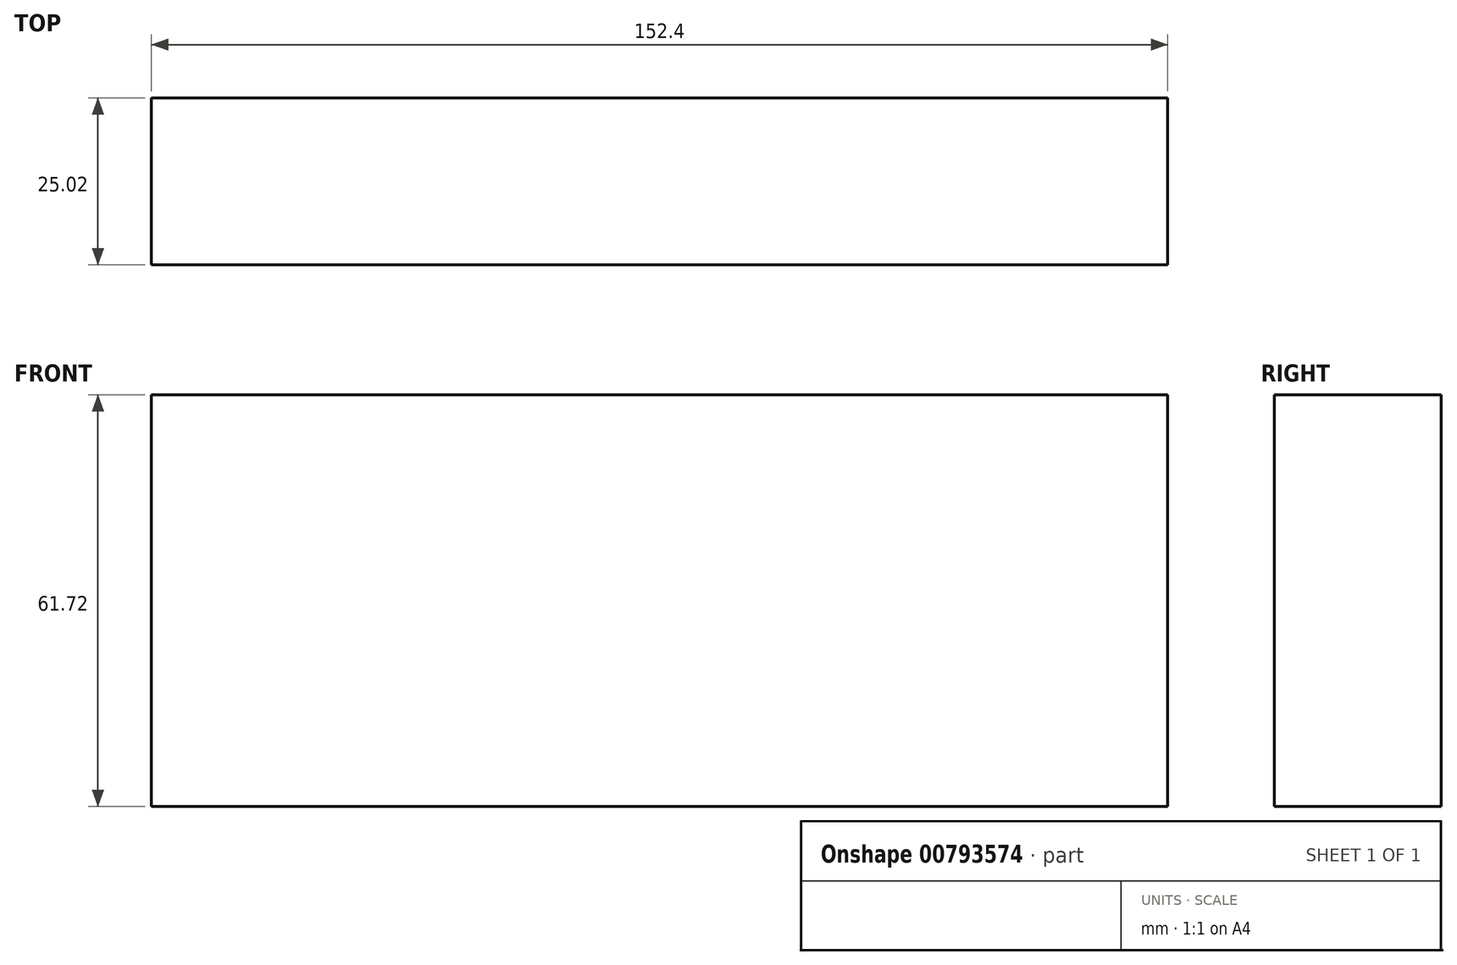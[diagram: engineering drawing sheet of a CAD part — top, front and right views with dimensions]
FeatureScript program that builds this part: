
annotation { "Feature Type Name" : "Feature", "Feature Type Description" : "" }
export const myFeature = defineFeature(function(context is Context, id is Id, definition is map)
    precondition{}
    {
        {
            var Q0;
            Q0=qCreatedBy(makeId("Front.planeOp"),FACE);
            var sketch = newSketch(context, id + "F0", { "sketchPlane" : qUnion([Q0])});
            skLineSegment(sketch, "E0.bottom", {"start": v(0, 0) * mm, "end": v(152.4, 0) * mm});
            skLineSegment(sketch, "E0.top", {"start": v(0, 61.72) * mm, "end": v(152.4, 61.72) * mm});
            skLineSegment(sketch, "E0.left", {"start": v(0, 0) * mm, "end": v(0, 61.72) * mm});
            skLineSegment(sketch, "E0.right", {"start": v(152.4, 0) * mm, "end": v(152.4, 61.72) * mm});
            skSolve(sketch);
        }
        {
            var Q0;
            Q0=qSketchRegion(id+"F0",true);
            extrude(context, id + "F1", {"entities" : qUnion([Q0]), "depth" : 25.02 * mm, "offsetDistance" : 25.4 * mm});
        }
    });
